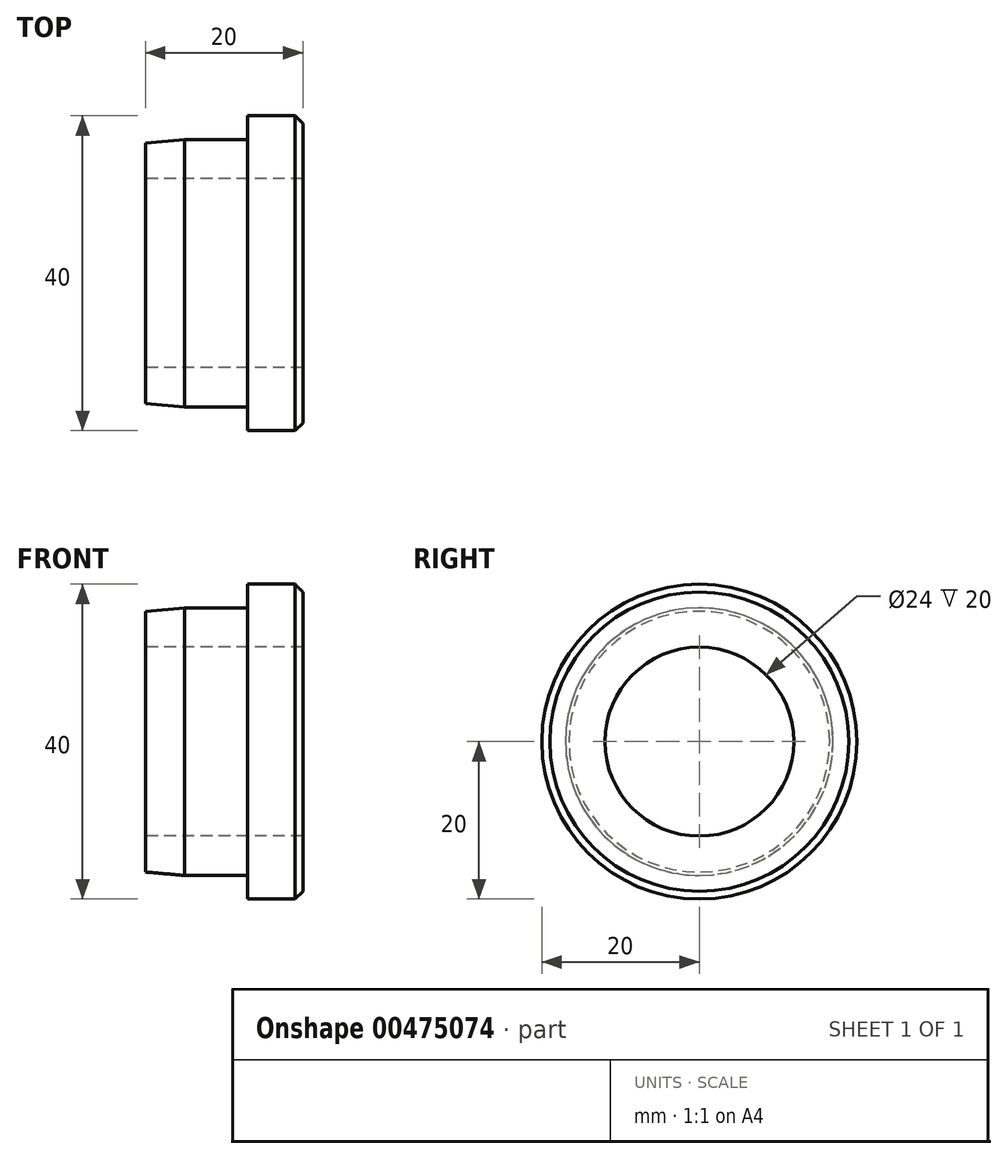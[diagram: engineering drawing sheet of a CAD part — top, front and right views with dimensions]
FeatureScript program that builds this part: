
annotation { "Feature Type Name" : "Feature", "Feature Type Description" : "" }
export const myFeature = defineFeature(function(context is Context, id is Id, definition is map)
    precondition{}
    {
        {
            var Q0;
            Q0=qCreatedBy(makeId("Front.planeOp"),FACE);
            var sketch = newSketch(context, id + "F0", { "sketchPlane" : qUnion([Q0])});
            skLineSegment(sketch, "E0", {"start": v(0, 0) * mm, "end": v(20, 0) * mm});
            skLineSegment(sketch, "E1", {"start": v(20, 0) * mm, "end": v(20, 20) * mm});
            skLineSegment(sketch, "E2", {"start": v(20, 20) * mm, "end": v(13, 20) * mm});
            skLineSegment(sketch, "E3", {"start": v(13, 20) * mm, "end": v(13, 17) * mm});
            skLineSegment(sketch, "E4", {"start": v(13, 17) * mm, "end": v(0, 17) * mm});
            skLineSegment(sketch, "E5", {"start": v(0, 17) * mm, "end": v(0, 0) * mm});
            skSolve(sketch);
        }
        {
            var Q0;
            Q0 = qSketchRegion(id + "F0", true);
            var Q1;
            Q1=sQuery(id+"F0.wireOp",EDGE,"E0");
            revolve(context, id + "F1", {"entities" : qUnion([Q0]), "axis" : qUnion([Q1]), "revolveType" : RevolveType.FULL});
        }
        {
            var Q0;
            Q0=makeQuery(id+"F1.opRevolve","SWEPT_EDGE",EDGE,{"disambiguationData":[OSD([sQuery(id+"F0.wireOp",EDGE,"E1"),sQuery(id+"F0.wireOp",EDGE,"E2")])]});
            chamfer(context, id + "F2", {"entities" : qUnion([Q0]), "width" : 1 * mm, "tangentPropagation" : true});
        }
        {
            var Q0;
            Q0=makeQuery(id+"F1.opRevolve","SWEPT_EDGE",EDGE,{"disambiguationData":[OSD([sQuery(id+"F0.wireOp",EDGE,"E4"),sQuery(id+"F0.wireOp",EDGE,"E5")])]});
            chamfer(context, id + "F3", {"entities" : qUnion([Q0]), "chamferType" : ChamferType.OFFSET_ANGLE, "width" : 5 * mm, "oppositeDirection" : true, "angle" : 5 * degree, "tangentPropagation" : true});
        }
        {
            var Q0;
            Q0=makeQuery(id+"F1.opRevolve","SWEPT_FACE",FACE,{"disambiguationData":[OSD([sQuery(id+"F0.wireOp",EDGE,"E5")])]});
            var sketch = newSketch(context, id + "F4", { "sketchPlane" : qUnion([Q0])});
            skCircle(sketch, "E6", {"center": v(0, 0) * mm, "radius": 12 * mm});
            skSolve(sketch);
        }
        {
            var Q0;
            Q0 = qSketchRegion(id + "F4", true);
            extrude(context, id + "F5", {"entities" : qUnion([Q0]), "operationType" : NewBodyOperationType.REMOVE, "oppositeDirection" : true, "depth" : 69.3 * mm});
        }
    });
